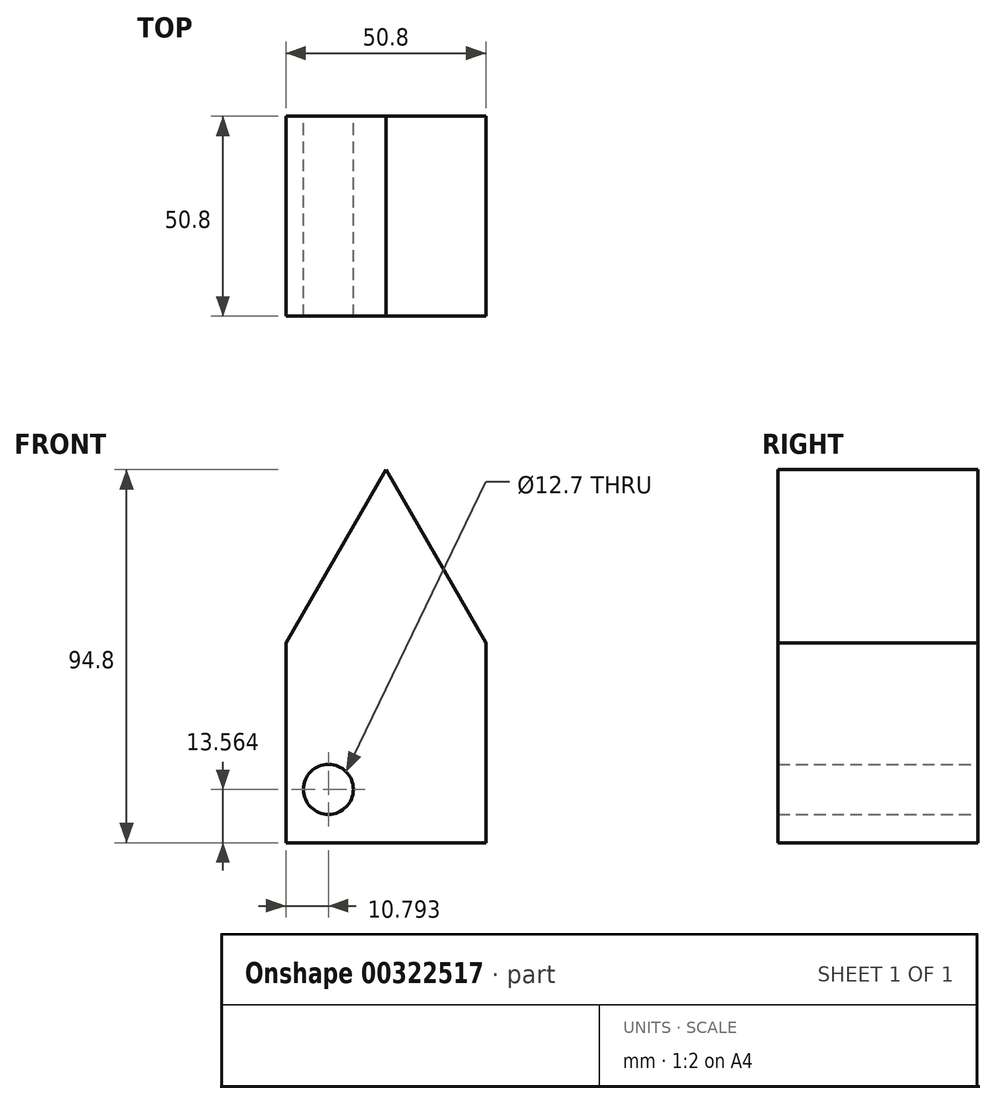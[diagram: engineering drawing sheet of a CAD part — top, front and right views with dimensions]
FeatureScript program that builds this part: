
annotation { "Feature Type Name" : "Feature", "Feature Type Description" : "" }
export const myFeature = defineFeature(function(context is Context, id is Id, definition is map)
    precondition{}
    {
        {
            var Q0;
            Q0=qCreatedBy(makeId("Front.planeOp"),FACE);
            var sketch = newSketch(context, id + "F0", { "sketchPlane" : qUnion([Q0])});
            skLineSegment(sketch, "E0.top", {"start": v(13.42, -47.08) * mm, "end": v(64.22, -47.08) * mm});
            skLineSegment(sketch, "E0.left", {"start": v(13.42, 3.72) * mm, "end": v(13.42, -47.08) * mm});
            skLineSegment(sketch, "E0.right", {"start": v(64.22, 3.72) * mm, "end": v(64.22, -47.08) * mm});
            skLineSegment(sketch, "E1", {"start": v(13.42, 3.72) * mm, "end": v(38.82, 47.72) * mm});
            skLineSegment(sketch, "E2", {"start": v(38.82, 47.72) * mm, "end": v(64.22, 3.72) * mm});
            skCircle(sketch, "E3", {"center": v(24.21, -33.52) * mm, "radius": 6.35 * mm});
            skSolve(sketch);
        }
        {
            var Q0;
            Q0=makeQuery(id+"F0.imprint","IMPRINT",FACE,{"disambiguationData":[TD([[makeQuery(id+"F0.imprint","IMPRINT",EDGE,{"derivedFrom":sQuery(id+"F0.wireOp",EDGE,"E0.top")}),1.0]])]});
            extrude(context, id + "F1", {"entities" : qUnion([Q0]), "depth" : 50.8 * mm});
        }
    });
